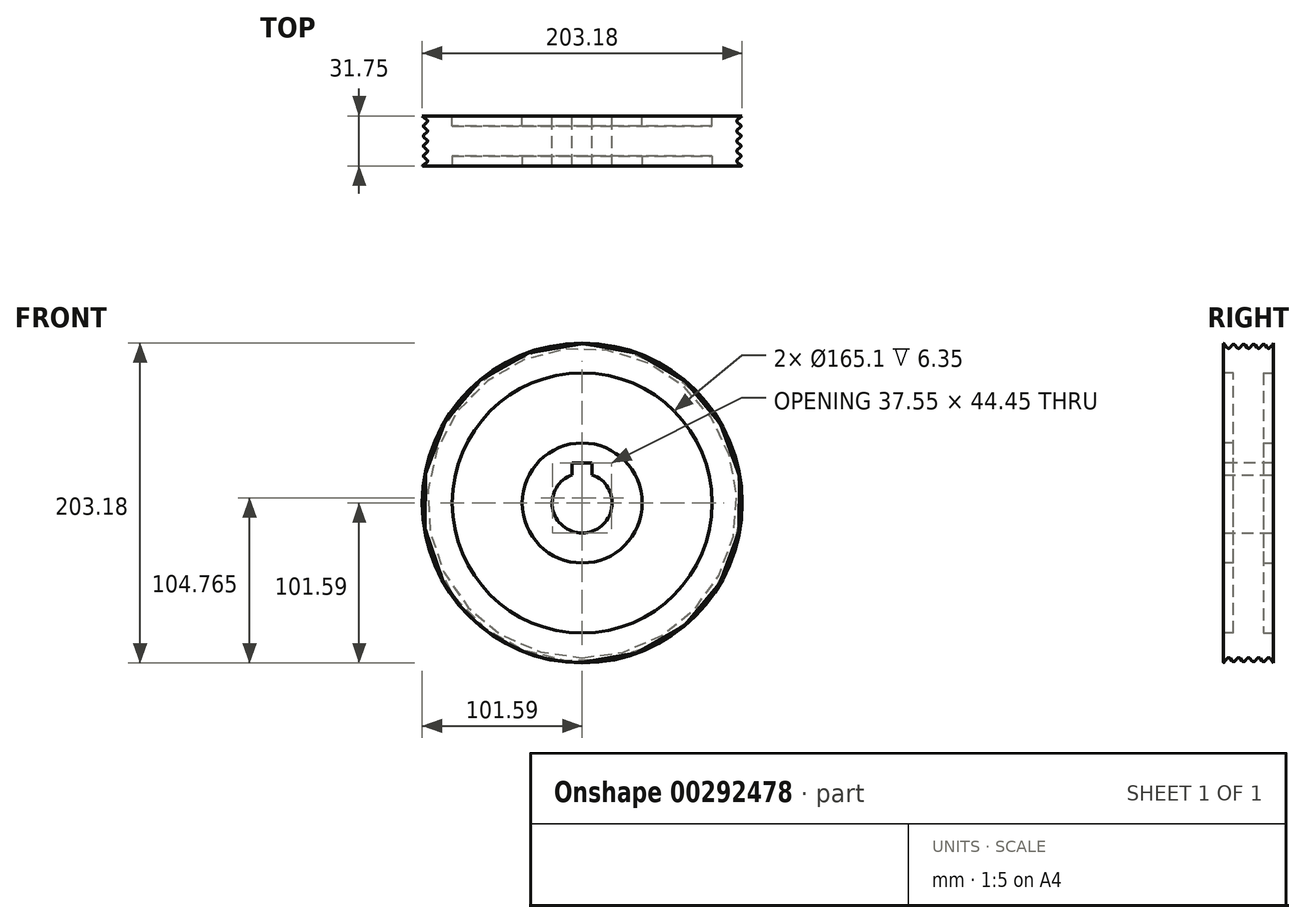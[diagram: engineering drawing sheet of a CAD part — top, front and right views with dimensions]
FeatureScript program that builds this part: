
annotation { "Feature Type Name" : "Feature", "Feature Type Description" : "" }
export const myFeature = defineFeature(function(context is Context, id is Id, definition is map)
    precondition{}
    {
        {
            var Q0;
            Q0=qCreatedBy(makeId("Front.planeOp"),FACE);
            var sketch = newSketch(context, id + "F0", { "sketchPlane" : qUnion([Q0])});
            skCircle(sketch, "E0", {"center": v(0, 0) * mm, "radius": 101.6 * mm});
            skCircle(sketch, "E1", {"center": v(0, 0) * mm, "radius": 19.05 * mm});
            skSolve(sketch);
        }
        {
            var Q0;
            Q0=makeQuery(id+"F0.imprint","IMPRINT",FACE,{"disambiguationData":[TD([[makeQuery(id+"F0.imprint","IMPRINT",EDGE,{"derivedFrom":sQuery(id+"F0.wireOp",EDGE,"E0")}),1.0]])]});
            extrude(context, id + "F1", {"entities" : qUnion([Q0]), "depth" : 31.75 * mm});
        }
        {
            var Q0;
            Q0=makeQuery(id+"F1.opExtrude","CAP_FACE",FACE,{"disambiguationData":[OSD([sQuery(id+"F0.wireOp",EDGE,"E0"),sQuery(id+"F0.wireOp",EDGE,"E1")])],"isStart":false});
            var sketch = newSketch(context, id + "F2", { "sketchPlane" : qUnion([Q0])});
            skCircle(sketch, "E2", {"center": v(0, 0) * mm, "radius": 38.1 * mm});
            skCircle(sketch, "E3", {"center": v(0, 0) * mm, "radius": 82.55 * mm});
            skSolve(sketch);
        }
        {
            var Q0;
            Q0=makeQuery(id+"F2.imprint","IMPRINT",FACE,{"disambiguationData":[TD([[makeQuery(id+"F2.imprint","IMPRINT",EDGE,{"derivedFrom":sQuery(id+"F2.wireOp",EDGE,"E2")}),-1.0]])]});
            extrude(context, id + "F3", {"entities" : qUnion([Q0]), "operationType" : NewBodyOperationType.REMOVE, "oppositeDirection" : true, "depth" : 6.35 * mm});
        }
        {
            var Q0;
            Q0=makeQuery(id+"F1.opExtrude","CAP_FACE",FACE,{"disambiguationData":[OSD([sQuery(id+"F0.wireOp",EDGE,"E0"),sQuery(id+"F0.wireOp",EDGE,"E1")])],"isStart":true});
            var sketch = newSketch(context, id + "F4", { "sketchPlane" : qUnion([Q0])});
            skCircle(sketch, "E4", {"center": v(0, 0) * mm, "radius": 38.1 * mm});
            skCircle(sketch, "E5", {"center": v(0, 0) * mm, "radius": 82.55 * mm});
            skSolve(sketch);
        }
        {
            var Q0;
            Q0 = qSketchRegion(id + "F4", true);
            extrude(context, id + "F5", {"entities" : qUnion([Q0]), "operationType" : NewBodyOperationType.REMOVE, "oppositeDirection" : true, "depth" : 6.35 * mm});
        }
        {
            var Q0;
            {var subQ0=sQuery(id+"F0.wireOp",EDGE,"E1");Q0=makeQuery(id+"F3.boolean.opBoolean","SPLIT",FACE,{"disambiguationData":[TD([makeQuery(id+"F1.opExtrude","SWEPT_FACE",FACE,{"disambiguationData":[OSD([subQ0])]})])],"derivedFrom":makeQuery(id+"F1.opExtrude","CAP_FACE",FACE,{"disambiguationData":[OSD([sQuery(id+"F0.wireOp",EDGE,"E0"),subQ0])],"isStart":false})});}
            var sketch = newSketch(context, id + "F6", { "sketchPlane" : qUnion([Q0])});
            skLineSegment(sketch, "E6.bottom", {"start": v(-6.35, 25.4) * mm, "end": v(6.35, 25.4) * mm});
            skLineSegment(sketch, "E6.top", {"start": v(-6.35, 12.7) * mm, "end": v(6.35, 12.7) * mm});
            skLineSegment(sketch, "E6.left", {"start": v(-6.35, 25.4) * mm, "end": v(-6.35, 12.7) * mm});
            skLineSegment(sketch, "E6.right", {"start": v(6.35, 25.4) * mm, "end": v(6.35, 12.7) * mm});
            skSolve(sketch);
        }
        {
            var Q0;
            Q0 = qSketchRegion(id + "F6", true);
            extrude(context, id + "F7", {"entities" : qUnion([Q0]), "operationType" : NewBodyOperationType.REMOVE, "endBound" : BoundingType.THROUGH_ALL, "oppositeDirection" : true, "depth" : 25.4 * mm});
        }
        {
            var Q0;
            Q0=qCreatedBy(makeId("Right.planeOp"),FACE);
            var sketch = newSketch(context, id + "F8", { "sketchPlane" : qUnion([Q0])});
            skLineSegment(sketch, "E7", {"start": v(0, 101.59) * mm, "end": v(-3.17, 97.46) * mm});
            skLineSegment(sketch, "E8", {"start": v(-3.17, 97.46) * mm, "end": v(-6.35, 101.59) * mm});
            skLineSegment(sketch, "E9", {"start": v(0, 113.59) * mm, "end": v(0, 101.59) * mm});
            skLineSegment(sketch, "E10", {"start": v(-6.35, 101.59) * mm, "end": v(-9.53, 97.46) * mm});
            skLineSegment(sketch, "E11", {"start": v(0, 101.59) * mm, "end": v(-31.78, 101.59) * mm, "construction": true});
            skLineSegment(sketch, "E12", {"start": v(-9.53, 97.46) * mm, "end": v(-12.7, 101.59) * mm});
            skLineSegment(sketch, "E13", {"start": v(-12.7, 101.59) * mm, "end": v(-15.9, 97.46) * mm});
            skLineSegment(sketch, "E14", {"start": v(-15.9, 97.46) * mm, "end": v(-19.08, 101.59) * mm});
            skLineSegment(sketch, "E15", {"start": v(-19.08, 101.59) * mm, "end": v(-22.25, 97.46) * mm});
            skLineSegment(sketch, "E16", {"start": v(-22.25, 97.46) * mm, "end": v(-25.43, 101.59) * mm});
            skLineSegment(sketch, "E17", {"start": v(-25.43, 101.59) * mm, "end": v(-28.6, 97.46) * mm});
            skLineSegment(sketch, "E18", {"start": v(-28.6, 97.46) * mm, "end": v(-31.78, 101.59) * mm});
            skLineSegment(sketch, "E19", {"start": v(0, 113.59) * mm, "end": v(-31.78, 113.59) * mm});
            skLineSegment(sketch, "E20", {"start": v(-31.78, 113.59) * mm, "end": v(-31.78, 101.59) * mm});
            skSolve(sketch);
        }
        {
            var Q0;
            Q0=makeQuery(id+"F8.imprint","IMPRINT",FACE,{"disambiguationData":[TD([[makeQuery(id+"F8.imprint","IMPRINT",EDGE,{"derivedFrom":sQuery(id+"F8.wireOp",EDGE,"E7")}),-1.0]])]});
            var Q1;
            Q1=makeQuery(id+"F1.opExtrude","SWEPT_FACE",FACE,{"disambiguationData":[OSD([sQuery(id+"F0.wireOp",EDGE,"E1")])]});
            revolve(context, id + "F9", {"operationType" : NewBodyOperationType.REMOVE, "entities" : qUnion([Q0]), "axis" : qUnion([Q1]), "revolveType" : RevolveType.FULL, "oppositeDirection" : true});
        }
        {
            var Q0;
            Q0=makeQuery(id+"F9.boolean.opBoolean","COPY",EDGE,{"derivedFrom":makeQuery(id+"F9.opRevolve","SWEPT_EDGE",EDGE,{"disambiguationData":[OSD([sQuery(id+"F8.wireOp",EDGE,"E7"),sQuery(id+"F8.wireOp",EDGE,"E9")])]})});
            var Q1;
            {var subQ0=sQuery(id+"F0.wireOp",EDGE,"E0");Q1=makeQuery(id+"F9.boolean.opBoolean","INTERSECT",EDGE,{"derivedFrom":[makeQuery(id+"F3.boolean.opBoolean","SPLIT",FACE,{"disambiguationData":[TD([makeQuery(id+"F1.opExtrude","SWEPT_FACE",FACE,{"disambiguationData":[OSD([subQ0])]})])],"derivedFrom":makeQuery(id+"F1.opExtrude","CAP_FACE",FACE,{"disambiguationData":[OSD([subQ0,sQuery(id+"F0.wireOp",EDGE,"E1")])],"isStart":false})}),makeQuery(id+"F9.opRevolve","SWEPT_FACE",FACE,{"disambiguationData":[OSD([sQuery(id+"F8.wireOp",EDGE,"E18")])]})]});}
            fillet(context, id + "F10", {"entities" : qUnion([Q0, Q1]), "radius" : 0.13 * mm, "tangentPropagation" : true, "allowEdgeOverflow" : false});
        }
        {
            var Q0;
            Q0=makeQuery(id+"F9.boolean.opBoolean","COPY",EDGE,{"derivedFrom":makeQuery(id+"F9.opRevolve","SWEPT_EDGE",EDGE,{"disambiguationData":[OSD([sQuery(id+"F8.wireOp",EDGE,"E7"),sQuery(id+"F8.wireOp",EDGE,"E8")])]})});
            var Q1;
            Q1=makeQuery(id+"F9.boolean.opBoolean","COPY",EDGE,{"derivedFrom":makeQuery(id+"F9.opRevolve","SWEPT_EDGE",EDGE,{"disambiguationData":[OSD([sQuery(id+"F8.wireOp",EDGE,"E10"),sQuery(id+"F8.wireOp",EDGE,"E12")])]})});
            var Q2;
            Q2=makeQuery(id+"F9.boolean.opBoolean","COPY",EDGE,{"derivedFrom":makeQuery(id+"F9.opRevolve","SWEPT_EDGE",EDGE,{"disambiguationData":[OSD([sQuery(id+"F8.wireOp",EDGE,"E13"),sQuery(id+"F8.wireOp",EDGE,"E14")])]})});
            var Q3;
            Q3=makeQuery(id+"F9.boolean.opBoolean","COPY",EDGE,{"derivedFrom":makeQuery(id+"F9.opRevolve","SWEPT_EDGE",EDGE,{"disambiguationData":[OSD([sQuery(id+"F8.wireOp",EDGE,"E15"),sQuery(id+"F8.wireOp",EDGE,"E16")])]})});
            var Q4;
            Q4=makeQuery(id+"F9.boolean.opBoolean","COPY",EDGE,{"derivedFrom":makeQuery(id+"F9.opRevolve","SWEPT_EDGE",EDGE,{"disambiguationData":[OSD([sQuery(id+"F8.wireOp",EDGE,"E17"),sQuery(id+"F8.wireOp",EDGE,"E18")])]})});
            var Q5;
            Q5=makeQuery(id+"F9.boolean.opBoolean","COPY",EDGE,{"derivedFrom":makeQuery(id+"F9.opRevolve","SWEPT_EDGE",EDGE,{"disambiguationData":[OSD([sQuery(id+"F8.wireOp",EDGE,"E16"),sQuery(id+"F8.wireOp",EDGE,"E17")])]})});
            var Q6;
            Q6=makeQuery(id+"F9.boolean.opBoolean","COPY",EDGE,{"derivedFrom":makeQuery(id+"F9.opRevolve","SWEPT_EDGE",EDGE,{"disambiguationData":[OSD([sQuery(id+"F8.wireOp",EDGE,"E14"),sQuery(id+"F8.wireOp",EDGE,"E15")])]})});
            var Q7;
            Q7=makeQuery(id+"F9.boolean.opBoolean","COPY",EDGE,{"derivedFrom":makeQuery(id+"F9.opRevolve","SWEPT_EDGE",EDGE,{"disambiguationData":[OSD([sQuery(id+"F8.wireOp",EDGE,"E12"),sQuery(id+"F8.wireOp",EDGE,"E13")])]})});
            var Q8;
            Q8=makeQuery(id+"F9.boolean.opBoolean","COPY",EDGE,{"derivedFrom":makeQuery(id+"F9.opRevolve","SWEPT_EDGE",EDGE,{"disambiguationData":[OSD([sQuery(id+"F8.wireOp",EDGE,"E8"),sQuery(id+"F8.wireOp",EDGE,"E10")])]})});
            fillet(context, id + "F11", {"entities" : qUnion([Q0, Q1, Q2, Q3, Q4, Q5, Q6, Q7, Q8]), "radius" : 1.27 * mm, "tangentPropagation" : true, "allowEdgeOverflow" : false});
        }
    });
